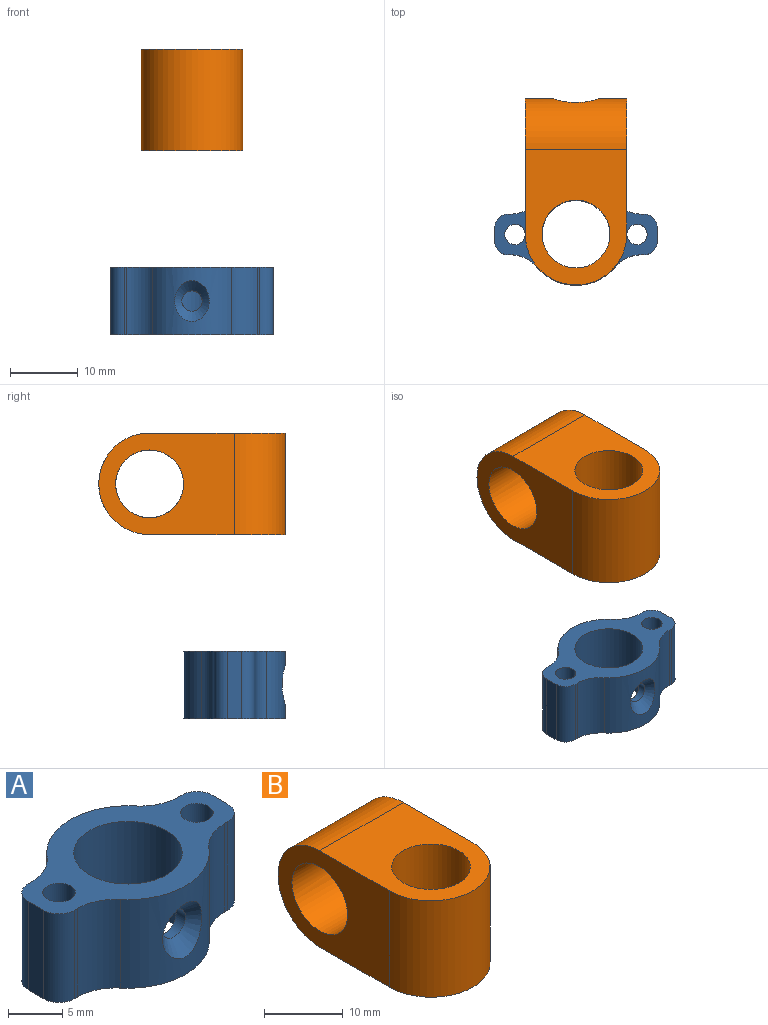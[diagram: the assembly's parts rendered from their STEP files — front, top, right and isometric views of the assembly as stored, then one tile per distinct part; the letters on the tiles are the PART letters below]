
ASSEMBLY  parts=2 mates=1
PART A: 23 faces, bbox 24x15x10 mm
  f0: cylinder r=7.5mm len=11.53mm, axis (0,0,-1), area 107.1mm2, adj f11,f12,f13,f14,f21
  f1: cylinder r=5mm len=10mm, axis (0,0,-1), area 307mm2, adj f11,f12,f22
  f2: plane 10x0.4mm, normal (0,-1,0), area 4mm2, adj f11,f12,f13,f20
  f3: plane 10x0.4mm, normal (0,-1,0), area 4mm2, adj f11,f12,f14,f17
  f4: plane 10x2mm, normal (1,0,0), area 20mm2, adj f11,f12,f17,f18
  f5: plane 10x0.4mm, normal (0,1,0), area 4mm2, adj f11,f12,f15,f18
  f6: cylinder r=7.5mm len=11.53mm, axis (0,0,-1), area 131.4mm2, adj f11,f12,f15,f16
  f7: plane 10x0.4mm, normal (0,1,0), area 4mm2, adj f11,f12,f16,f19
  f8: cylinder r=1.5mm len=10mm, axis (0,0,-1), area 94.2mm2, adj f11,f12
  f9: cylinder r=1.5mm len=10mm, axis (0,0,-1), area 94.2mm2, adj f11,f12
  f10: plane 10x2mm, normal (-1,0,0), area 20mm2, adj f11,f12,f19,f20
  f11: plane 24x15mm, normal (0,0,1), area 141.1mm2, adj f0,f1,f2,f3,f4,f5,f6,f7
  f12: plane 24x15mm, normal (0,0,-1), area 141.1mm2, adj f0,f1,f2,f3,f4,f5,f6,f7
  f13: cylinder r=5mm len=10mm, axis (0,0,-1), area 43.8mm2, adj f0,f2,f11,f12
  f14: cylinder r=5mm len=10mm, axis (0,0,-1), area 43.8mm2, adj f0,f3,f11,f12
  f15: cylinder r=5mm len=10mm, axis (0,0,-1), area 43.8mm2, adj f5,f6,f11,f12
  f16: cylinder r=5mm len=10mm, axis (0,0,-1), area 43.8mm2, adj f6,f7,f11,f12
  f17: cylinder r=2mm len=10mm, axis (0,0,-1), area 31.4mm2, adj f3,f4,f11,f12
  f18: cylinder r=2mm len=10mm, axis (0,0,1), area 31.4mm2, adj f4,f5,f11,f12
  f19: cylinder r=2mm len=10mm, axis (0,0,-1), area 31.4mm2, adj f7,f10,f11,f12
  f20: cylinder r=2mm len=10mm, axis (0,0,1), area 31.4mm2, adj f2,f10,f11,f12
  f21: cone r=1.5mm half-angle=45deg, axis (0,-1,0), area 24mm2, adj f0,f22
  f22: cylinder r=1.5mm len=3mm, axis (0,-1,0), area 10.5mm2, adj f1,f21
PART B: 10 faces, bbox 15x27.5x15 mm
  f0: cylinder r=5mm len=15mm, axis (1,0,0), area 464.1mm2, adj f3,f4,f8
  f1: cylinder r=7.5mm len=15mm, axis (1,0,0), area 320.8mm2, adj f3,f4,f6,f7,f9
  f2: cylinder r=7.5mm len=15mm, axis (0,0,-1), area 354mm2, adj f3,f4,f6,f7
  f3: plane 20x15mm, normal (1,0,0), area 197.3mm2, adj f0,f1,f2,f6,f7
  f4: plane 19.96x15mm, normal (-1,0,0), area 196.7mm2, adj f0,f1,f2,f6,f7
  f5: cylinder r=5mm len=15mm, axis (0,0,-1), area 471.2mm2, adj f6,f7
  f6: plane 20x15mm, normal (0,0,1), area 197.3mm2, adj f1,f2,f3,f4,f5
  f7: plane 20x15mm, normal (0,0,-1), area 197.3mm2, adj f1,f2,f3,f4,f5
  f8: cylinder r=1.5mm len=3mm, axis (0,1,0), area 5.8mm2, adj f0,f9
  f9: cone r=1.5mm half-angle=45deg, axis (0,1,0), area 35.2mm2, adj f1,f8
PLACE A at identity fixed
PLACE B t=(0,0,27.18)mm
MATE cylindrical B.f5 <-> A.f1  axis (0,0,-1) through (0,0,27.18)mm
